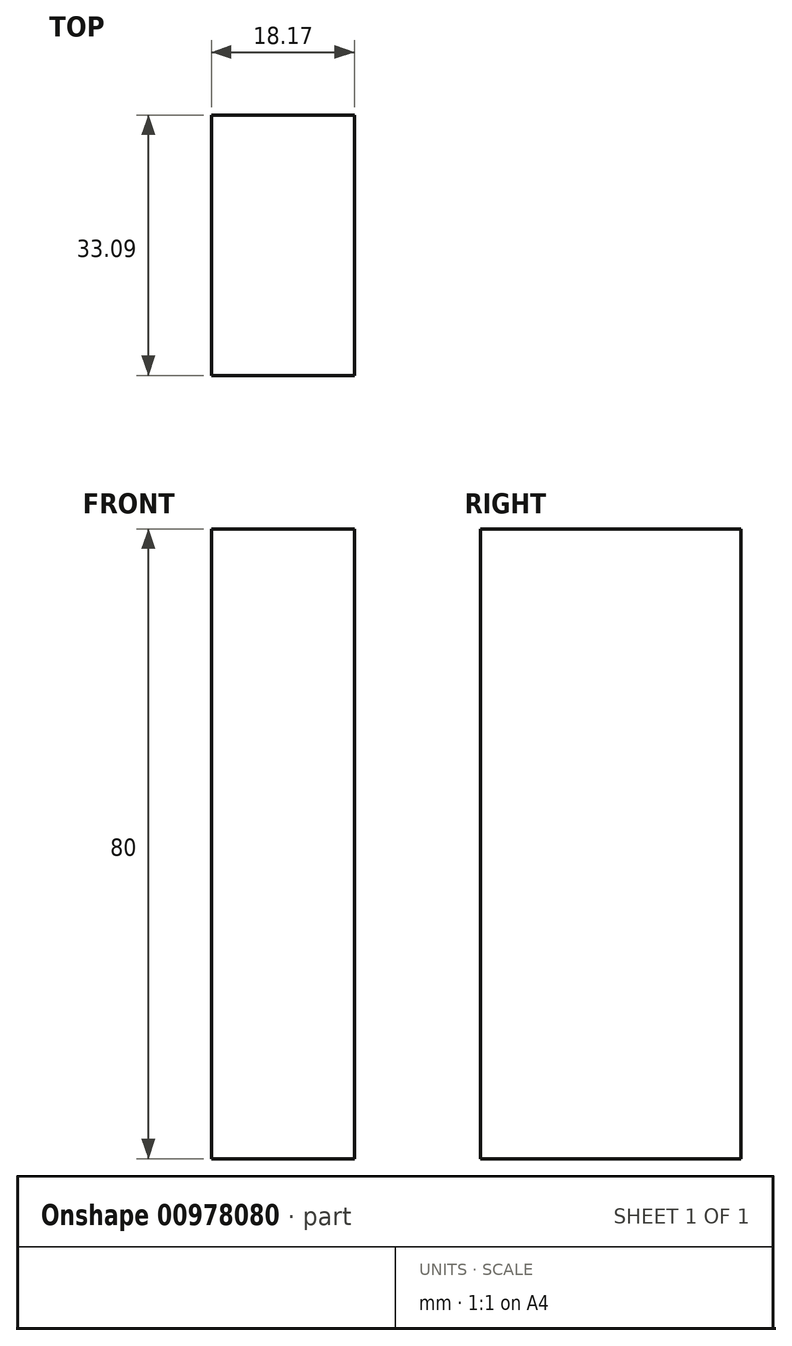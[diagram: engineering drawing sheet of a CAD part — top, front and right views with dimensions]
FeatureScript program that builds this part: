
annotation { "Feature Type Name" : "Feature", "Feature Type Description" : "" }
export const myFeature = defineFeature(function(context is Context, id is Id, definition is map)
    precondition{}
    {
        {
            var Q0;
            Q0=qCreatedBy(makeId("Top.planeOp"),FACE);
            var sketch = newSketch(context, id + "F0", { "sketchPlane" : qUnion([Q0])});
            skLineSegment(sketch, "E0.bottom", {"start": v(18.17, 33.09) * mm, "end": v(0, 33.09) * mm});
            skLineSegment(sketch, "E0.top", {"start": v(18.17, 0) * mm, "end": v(0, 0) * mm});
            skLineSegment(sketch, "E0.left", {"start": v(18.17, 33.09) * mm, "end": v(18.17, 0) * mm});
            skLineSegment(sketch, "E0.right", {"start": v(0, 33.09) * mm, "end": v(0, 0) * mm});
            skSolve(sketch);
        }
        {
            var Q0;
            Q0 = qSketchRegion(id + "F0", true);
            extrude(context, id + "F1", {"entities" : qUnion([Q0]), "depth" : 750 * mm, "offsetDistance" : 25 * mm});
        }
        {
            var Q0;
            Q0=makeQuery(id+"F0.imprint","IMPRINT",FACE,{"disambiguationData":[TD([[makeQuery(id+"F0.imprint","IMPRINT",EDGE,{"derivedFrom":sQuery(id+"F0.wireOp",EDGE,"E0.bottom")}),1.0]])]});
            var Q1;
            Q1 = qSketchRegion(id + "F0", true);
            extrude(context, id + "F2", {"entities" : qUnion([Q0, Q1]), "operationType" : NewBodyOperationType.INTERSECT, "depth" : 80 * mm, "offsetDistance" : 25 * mm});
        }
    });
